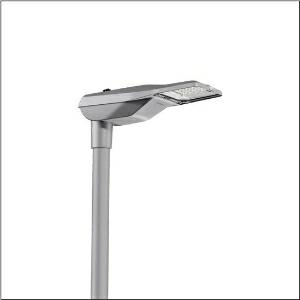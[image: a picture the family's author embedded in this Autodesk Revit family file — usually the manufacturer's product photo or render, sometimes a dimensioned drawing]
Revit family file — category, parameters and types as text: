
# Revit family: streetlight_sl_21_micro___p0_8ab_5xe1r33s08db_200d
name_source: partatom
category: Lighting Fixtures
units: mm (PartAtom-declared; Revit-internal decimal feet)

## family parameters
Cut with Voids When Loaded = No
Host = Face
Light Source = No
Part Type = Normal
Room Calculation Point = No
Round Connector Dimension = Use Diameter
Shared = No

## types (1)
- --- (1 x LED, 4470 lm, 39.1 W, 3000K)
    Apparent Load = 39 VA
    CIE Flux Codes = 36 71 98 100 100
    Color Rendering = 70
    Color Temperature = 3000K
    Default Elevation = 1800 mm
    Description = Streetlight SL 21 micro, mast luminaire, primary light control with lens, of PMMA, primary optical cover: cover, of toughened safety glass, transparent, light distribution: P0.8aB, light emission: direct distribution, primary light characteristic: asymmetric, installation type: post-top, side-entry, LED, High Power LED, rated luminous flux: 4.470lm, luminous efficacy: 114lm/W, light colour: 730, colour temperature: 3000K, control gear: D4i, control: pre-setting: logarithmic dimming characteristic, flexible luminous flux parameterisation, time-dependent luminous flux control, constant luminous flux control, overheat protection, mains connection: 220..240V, AC, 50/60Hz, start of lifetime: 39W, end of service life: 41W, reduction: 18W, luminaire housing, of diecast aluminium, powder-coated, Siteco® metallic grey (DB 702S), corrosivity category C5 mid according to DIN EN ISO 12944, multi-level sealing system, sealing non-destructively replaceable, inclination adjustable: 0°, 5°, 10°, 15°, please order mast flange separately, length: 528mm, width: 235mm, height: 110mm, mast flange for spigot size: 42mm (side-entry): 5XC10008XM4, 60/48mm (side-entry/post-top): 5XC10108XM2, 76/60mm (side-entry/post-top): 5XC10108XM1, Smart Interface above, protection rating (complete): IP66, insulation class (complete): insulation class II (safety insulation), certification: CE, ENEC, ENEC+, VDE, impact resistance: IK10, permissible operating ambient temperature for outdoor applications: -40..+50°C, standard-compliant lighting for roads and squares, packaging unit: 1 piece

Light Distribution: P0.8aB
    Height = 110 mm
    Lamp = 1 x LED
    Lamp Light Flux = 4470 lm
    Lamp Power = 39.1 W
    Lamp count = 1
    Length = 528 mm
    Luminous efficacy = 114 lm/W
    Manufacturer = Siteco
    ModVariant = No
    Model = 5XE1R33S08DB
    Number of Poles = 1
    OnlyDefault = Yes
    Power Factor = 1
    Product Name = Streetlight SL 21 micro | P0.8aB
    Product group = mast luminaire | pylon top
    ProductGroupID = 6100
    Protection Class = Protection class II
    Protection Degree = IP 66
    RLX_Detail_Level = 1
    RLX_Emergency_Light_Flux = 0 lm
    RLX_Emergency_Type = 0
    RLX_Emergency_Type_DB = No
    RlxData = <blob elided: 98081 chars, md5=d7d491f7>
    Socket = socket
    Standby Power = 0 W
    System Light Flux = 4470 lm
    System Power = 39 W
    Type Comments = factory setting: luminous flux: 100 % | dim-lin: 254 | 765 mA
    Type Image = l_1277292.jpg
    URL = http://relux.com
    VarID = @adj_075120
    Voltage = 0 V
    Weight = 0.00 kg
    Width = 235 mm

## geometry (parser evidence)
native form markers: Blend x4, Sweep x12
no freeform markers — native parametric forms only
